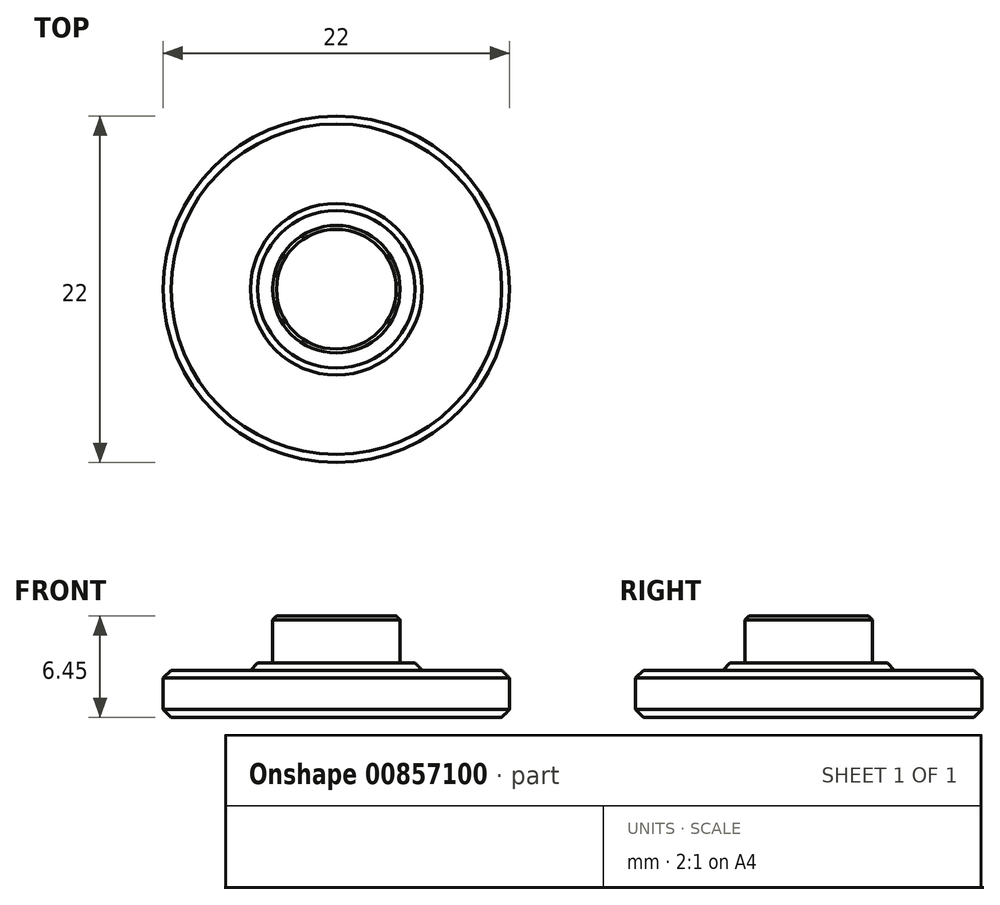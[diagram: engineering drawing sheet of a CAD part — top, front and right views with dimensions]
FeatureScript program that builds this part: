
annotation { "Feature Type Name" : "Feature", "Feature Type Description" : "" }
export const myFeature = defineFeature(function(context is Context, id is Id, definition is map)
    precondition{}
    {
        {
            var Q0;
            Q0=qCreatedBy(makeId("Top.planeOp"),FACE);
            var sketch = newSketch(context, id + "F0", { "sketchPlane" : qUnion([Q0])});
            skCircle(sketch, "E0", {"center": v(0, 0) * mm, "radius": 11 * mm});
            skSolve(sketch);
        }
        {
            var Q0;
            Q0=qSketchRegion(id+"F0",true);
            extrude(context, id + "F1", {"entities" : qUnion([Q0]), "depth" : 3 * mm, "offsetDistance" : 25 * mm});
        }
        {
            var Q0;
            Q0=makeQuery(id+"F1.opExtrude","CAP_FACE",FACE,{"disambiguationData":[OSD([sQuery(id+"F0.wireOp",EDGE,"E0")])],"isStart":false});
            var sketch = newSketch(context, id + "F2", { "sketchPlane" : qUnion([Q0])});
            skCircle(sketch, "E1", {"center": v(0, 0) * mm, "radius": 5.5 * mm});
            skSolve(sketch);
        }
        {
            var Q0;
            Q0=qSketchRegion(id+"F2",true);
            extrude(context, id + "F3", {"entities" : qUnion([Q0]), "operationType" : NewBodyOperationType.ADD, "depth" : 0.45 * mm, "offsetDistance" : 25 * mm});
        }
        {
            var Q0;
            Q0=makeQuery(id+"F3.opExtrude","CAP_FACE",FACE,{"disambiguationData":[OSD([sQuery(id+"F2.wireOp",EDGE,"E1")])],"isStart":false});
            var sketch = newSketch(context, id + "F4", { "sketchPlane" : qUnion([Q0])});
            skCircle(sketch, "E2", {"center": v(0, 0) * mm, "radius": 4.05 * mm});
            skSolve(sketch);
        }
        {
            var Q0;
            Q0=qSketchRegion(id+"F4",true);
            extrude(context, id + "F5", {"entities" : qUnion([Q0]), "operationType" : NewBodyOperationType.ADD, "depth" : 3 * mm, "offsetDistance" : 25 * mm});
        }
        {
            var Q0;
            Q0=makeQuery(id+"F5.opExtrude","CAP_EDGE",EDGE,{"disambiguationData":[OSD([sQuery(id+"F4.wireOp",EDGE,"E2")])],"isStart":false});
            chamfer(context, id + "F6", {"entities" : qUnion([Q0]), "width" : 0.25 * mm, "tangentPropagation" : true});
        }
        {
            var Q0;
            Q0=makeQuery(id+"F3.opExtrude","CAP_EDGE",EDGE,{"disambiguationData":[OSD([sQuery(id+"F2.wireOp",EDGE,"E1")])],"isStart":false});
            chamfer(context, id + "F7", {"entities" : qUnion([Q0]), "width" : 0.5 * mm, "tangentPropagation" : true});
        }
        {
            var Q0;
            Q0=makeQuery(id+"F1.opExtrude","CAP_EDGE",EDGE,{"disambiguationData":[OSD([sQuery(id+"F0.wireOp",EDGE,"E0")])],"isStart":true});
            var Q1;
            Q1=makeQuery(id+"F1.opExtrude","CAP_EDGE",EDGE,{"disambiguationData":[OSD([sQuery(id+"F0.wireOp",EDGE,"E0")])],"isStart":false});
            chamfer(context, id + "F8", {"entities" : qUnion([Q0, Q1]), "width" : 0.5 * mm, "tangentPropagation" : true});
        }
    });
